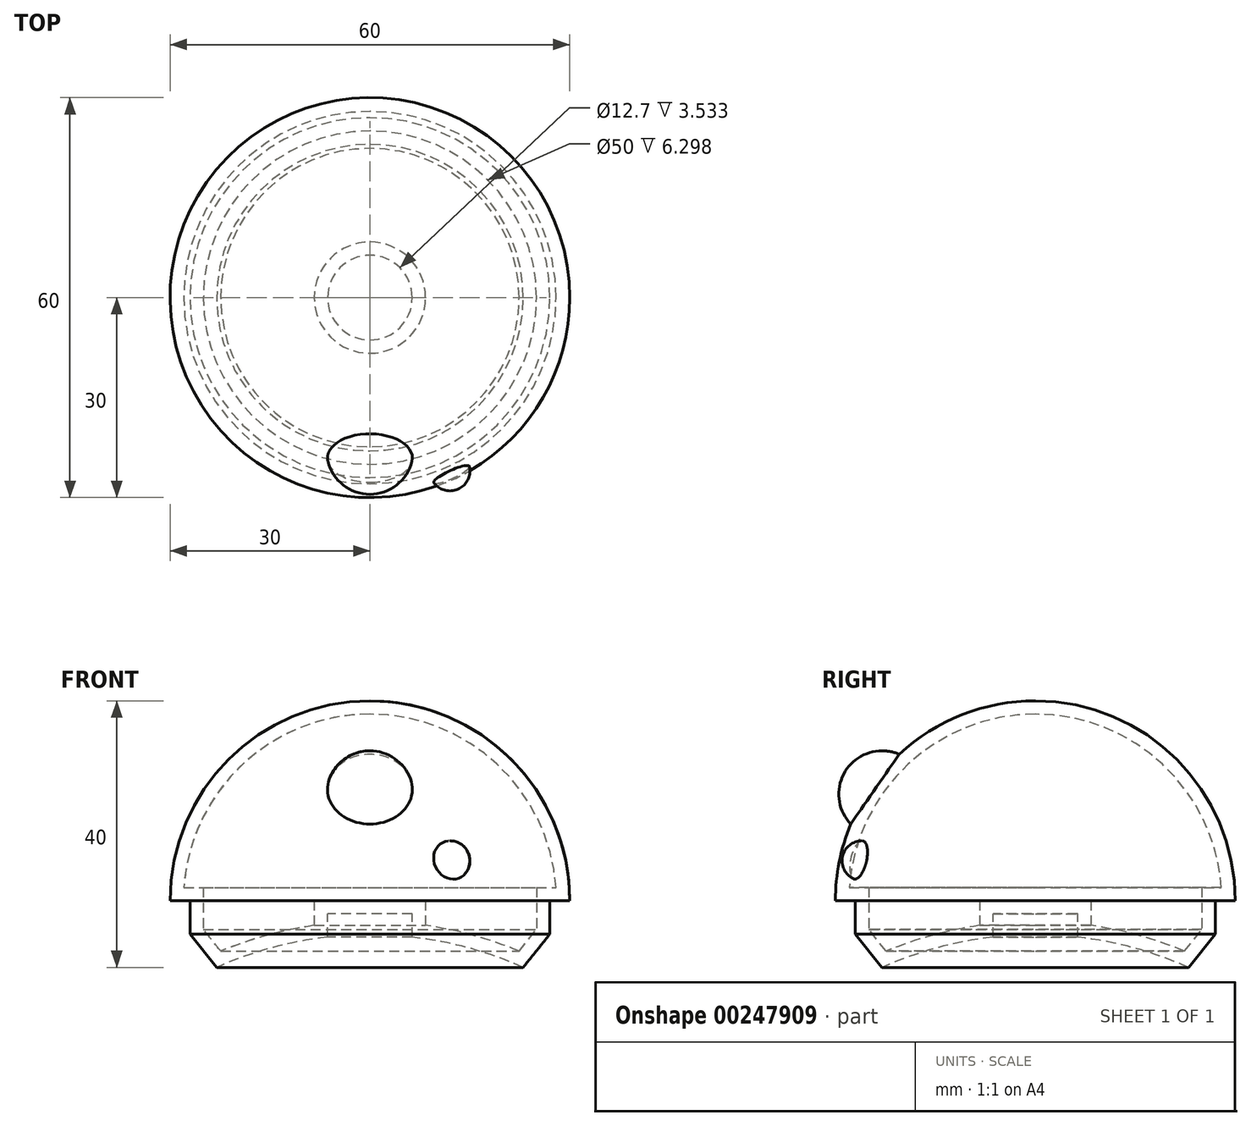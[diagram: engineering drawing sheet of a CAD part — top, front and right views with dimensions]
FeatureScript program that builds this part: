
annotation { "Feature Type Name" : "Feature", "Feature Type Description" : "" }
export const myFeature = defineFeature(function(context is Context, id is Id, definition is map)
    precondition{}
    {
        {
            var Q0;
            Q0=qCreatedBy(makeId("Front.planeOp"),FACE);
            var sketch = newSketch(context, id + "F0", { "sketchPlane" : qUnion([Q0])});
            skArc(sketch, "E0", {"start": v(-27.4, -12.2) * mm, "mid": v(0, -30) * mm, "end": v(27.4, -12.2) * mm});
            skLineSegment(sketch, "E1", {"start": v(-27, 0) * mm, "end": v(-30, 0) * mm});
            skLineSegment(sketch, "E2", {"start": v(-27, 0) * mm, "end": v(-27, -5) * mm});
            skLineSegment(sketch, "E3", {"start": v(0, 0) * mm, "end": v(0, -1.93) * mm});
            skLineSegment(sketch, "E4", {"start": v(0, -10) * mm, "end": v(-23, -10) * mm});
            skLineSegment(sketch, "E5", {"start": v(-23, -10) * mm, "end": v(-27, -5) * mm});
            skArc(sketch, "E6", {"start": v(-6.35, -5.46) * mm, "mid": v(-14.85, -7.1) * mm, "end": v(-23, -10) * mm});
            skLineSegment(sketch, "E7", {"start": v(0, 30) * mm, "end": v(0, -1.93) * mm});
            skLineSegment(sketch, "E8.bottom", {"start": v(0, -10) * mm, "end": v(-6.35, -10) * mm});
            skLineSegment(sketch, "E8.top", {"start": v(0, -1.93) * mm, "end": v(-6.35, -1.93) * mm});
            skLineSegment(sketch, "E8.left", {"start": v(0, -10) * mm, "end": v(0, -5.1) * mm});
            skLineSegment(sketch, "E8.right", {"start": v(-6.35, -5.46) * mm, "end": v(-6.35, -1.93) * mm});
            skArc(sketch, "E9.trimOffspring", {"start": v(0, 30) * mm, "mid": v(-21.21, 21.21) * mm, "end": v(-30, 0) * mm});
            skLineSegment(sketch, "E10.trimOffspring", {"start": v(0, -5.1) * mm, "end": v(0, -10) * mm});
            skArc(sketch, "E11.trimOffspring", {"start": v(-27.4, -12.2) * mm, "mid": v(14.16, -116.3) * mm, "end": v(0, -5.1) * mm});
            skLineSegment(sketch, "E12.0", {"start": v(0, 0.07) * mm, "end": v(-8.35, 0.07) * mm});
            skLineSegment(sketch, "E12.1", {"start": v(-8.35, -3.7) * mm, "end": v(-8.35, 0.07) * mm});
            skArc(sketch, "E12.2", {"start": v(-8.35, -3.7) * mm, "mid": v(-15.5, -5.2) * mm, "end": v(-22.39, -7.56) * mm});
            skArc(sketch, "E12.3", {"start": v(0, 28) * mm, "mid": v(-19.08, 20.5) * mm, "end": v(-27.93, 2) * mm});
            skLineSegment(sketch, "E12.4", {"start": v(-25, 2) * mm, "end": v(-27.93, 2) * mm});
            skLineSegment(sketch, "E12.5", {"start": v(-25, 2) * mm, "end": v(-25, -4.3) * mm});
            skLineSegment(sketch, "E12.6", {"start": v(-22.39, -7.56) * mm, "end": v(-25, -4.3) * mm});
            skSolve(sketch);
        }
        {
            var Q0;
            {var subQ0=sQuery(id+"F0.wireOp",EDGE,"E12.0");Q0=makeQuery(id+"F0.imprint","IMPRINT",FACE,{"disambiguationData":[TD([[makeQuery(id+"F0.imprint","IMPRINT",EDGE,{"derivedFrom":subQ0}),-1.0]])]});}
            var Q1;
            Q1=makeQuery(id+"F0.imprint","IMPRINT",FACE,{"disambiguationData":[TD([[makeQuery(id+"F0.imprint","IMPRINT",EDGE,{"derivedFrom":sQuery(id+"F0.wireOp",EDGE,"E1")}),-1.0]])]});
            var Q2;
            Q2=sQuery(id+"F0.wireOp",EDGE,"E7");
            revolve(context, id + "F1", {"entities" : qUnion([Q0, Q1]), "axis" : qUnion([Q2]), "revolveType" : RevolveType.FULL});
        }
        {
            var Q0;
            Q0=qCreatedBy(makeId("Front.planeOp"),FACE);
            cPlane(context, id + "F2", {"entities" : qUnion([Q0]), "cplaneType" : CPlaneType.OFFSET, "offset" : 23 * mm, "width" : 150 * mm, "height" : 150 * mm});
        }
        {
            var Q0;
            Q0=qCreatedBy(id+"F2.planeOp",FACE);
            var sketch = newSketch(context, id + "F3", { "sketchPlane" : qUnion([Q0])});
            skArc(sketch, "E13", {"start": v(0, 9.5) * mm, "mid": v(6.5, 16) * mm, "end": v(0, 22.5) * mm});
            skLineSegment(sketch, "E14", {"start": v(0, 22.5) * mm, "end": v(0, 9.5) * mm});
            skSolve(sketch);
        }
        {
            var Q0;
            Q0=makeQuery(id+"F3.imprint","IMPRINT",FACE,{"disambiguationData":[TD([[makeQuery(id+"F3.imprint","IMPRINT",EDGE,{"derivedFrom":sQuery(id+"F3.wireOp",EDGE,"E13")}),1.0]])]});
            var Q1;
            Q1=sQuery(id+"F3.wireOp",EDGE,"E14");
            revolve(context, id + "F4", {"operationType" : NewBodyOperationType.ADD, "entities" : qUnion([Q0]), "axis" : qUnion([Q1]), "revolveType" : RevolveType.FULL});
        }
        {
            var Q0;
            Q0=qCreatedBy(makeId("Front.planeOp"),FACE);
            cPlane(context, id + "F5", {"entities" : qUnion([Q0]), "cplaneType" : CPlaneType.OFFSET, "offset" : 26 * mm, "width" : 150 * mm, "height" : 150 * mm});
        }
        {
            var Q0;
            Q0=qCreatedBy(id+"F5.planeOp",FACE);
            var sketch = newSketch(context, id + "F6", { "sketchPlane" : qUnion([Q0])});
            skArc(sketch, "E15", {"start": v(12, 3) * mm, "mid": v(15, 6) * mm, "end": v(12, 9) * mm});
            skLineSegment(sketch, "E16.0", {"start": v(-30, 0) * mm, "end": v(30, 0) * mm});
            skLineSegment(sketch, "E17", {"start": v(12, 9) * mm, "end": v(12, 3) * mm});
            skSolve(sketch);
        }
        {
            var Q0;
            Q0 = qSketchRegion(id + "F6", true);
            var Q1;
            Q1=sQuery(id+"F6.wireOp",EDGE,"E17");
            revolve(context, id + "F7", {"operationType" : NewBodyOperationType.ADD, "entities" : qUnion([Q0]), "axis" : qUnion([Q1]), "revolveType" : RevolveType.FULL});
        }
        {
            var Q0;
            Q0=qCreatedBy(makeId("Front.planeOp"),FACE);
            var sketch = newSketch(context, id + "F8", { "sketchPlane" : qUnion([Q0])});
            skLineSegment(sketch, "E18", {"start": v(0, 30) * mm, "end": v(0, -1.93) * mm});
            skArc(sketch, "E19", {"start": v(0, 30) * mm, "mid": v(-21.21, 21.21) * mm, "end": v(-30, 0) * mm});
            skLineSegment(sketch, "E20.0", {"start": v(-30, 0) * mm, "end": v(-27, 0) * mm});
            skLineSegment(sketch, "E21", {"start": v(-27, -5) * mm, "end": v(-27, 0) * mm});
            skLineSegment(sketch, "E22", {"start": v(-23, -10) * mm, "end": v(-27, -5) * mm});
            skArc(sketch, "E23", {"start": v(-6.35, -5.46) * mm, "mid": v(-14.85, -7.1) * mm, "end": v(-23, -10) * mm});
            skLineSegment(sketch, "E24.0", {"start": v(-6.35, -1.93) * mm, "end": v(0, -1.93) * mm});
            skLineSegment(sketch, "E25", {"start": v(-6.35, -1.93) * mm, "end": v(-6.35, -5.46) * mm});
            skLineSegment(sketch, "E26.0", {"start": v(-8.35, 0.07) * mm, "end": v(0, 0.07) * mm});
            skLineSegment(sketch, "E26.1", {"start": v(-8.35, 0.07) * mm, "end": v(-8.35, -3.7) * mm});
            skArc(sketch, "E26.2", {"start": v(-8.35, -3.7) * mm, "mid": v(-15.5, -5.2) * mm, "end": v(-22.39, -7.56) * mm});
            skArc(sketch, "E26.3", {"start": v(0, 28) * mm, "mid": v(-19.08, 20.5) * mm, "end": v(-27.93, 2) * mm});
            skLineSegment(sketch, "E26.4", {"start": v(-27.93, 2) * mm, "end": v(-25, 2) * mm});
            skLineSegment(sketch, "E26.5", {"start": v(-25, -4.3) * mm, "end": v(-25, 2) * mm});
            skLineSegment(sketch, "E26.6", {"start": v(-22.39, -7.56) * mm, "end": v(-25, -4.3) * mm});
            skSolve(sketch);
        }
        {
            var Q0;
            {var subQ0=sQuery(id+"F8.wireOp",EDGE,"E26.0");Q0=makeQuery(id+"F8.imprint","IMPRINT",FACE,{"disambiguationData":[TD([[makeQuery(id+"F8.imprint","IMPRINT",EDGE,{"derivedFrom":subQ0}),1.0]])]});}
            var Q1;
            Q1=sQuery(id+"F8.wireOp",EDGE,"E18");
            revolve(context, id + "F9", {"operationType" : NewBodyOperationType.REMOVE, "entities" : qUnion([Q0]), "axis" : qUnion([Q1]), "revolveType" : RevolveType.FULL, "oppositeDirection" : true});
        }
    });
